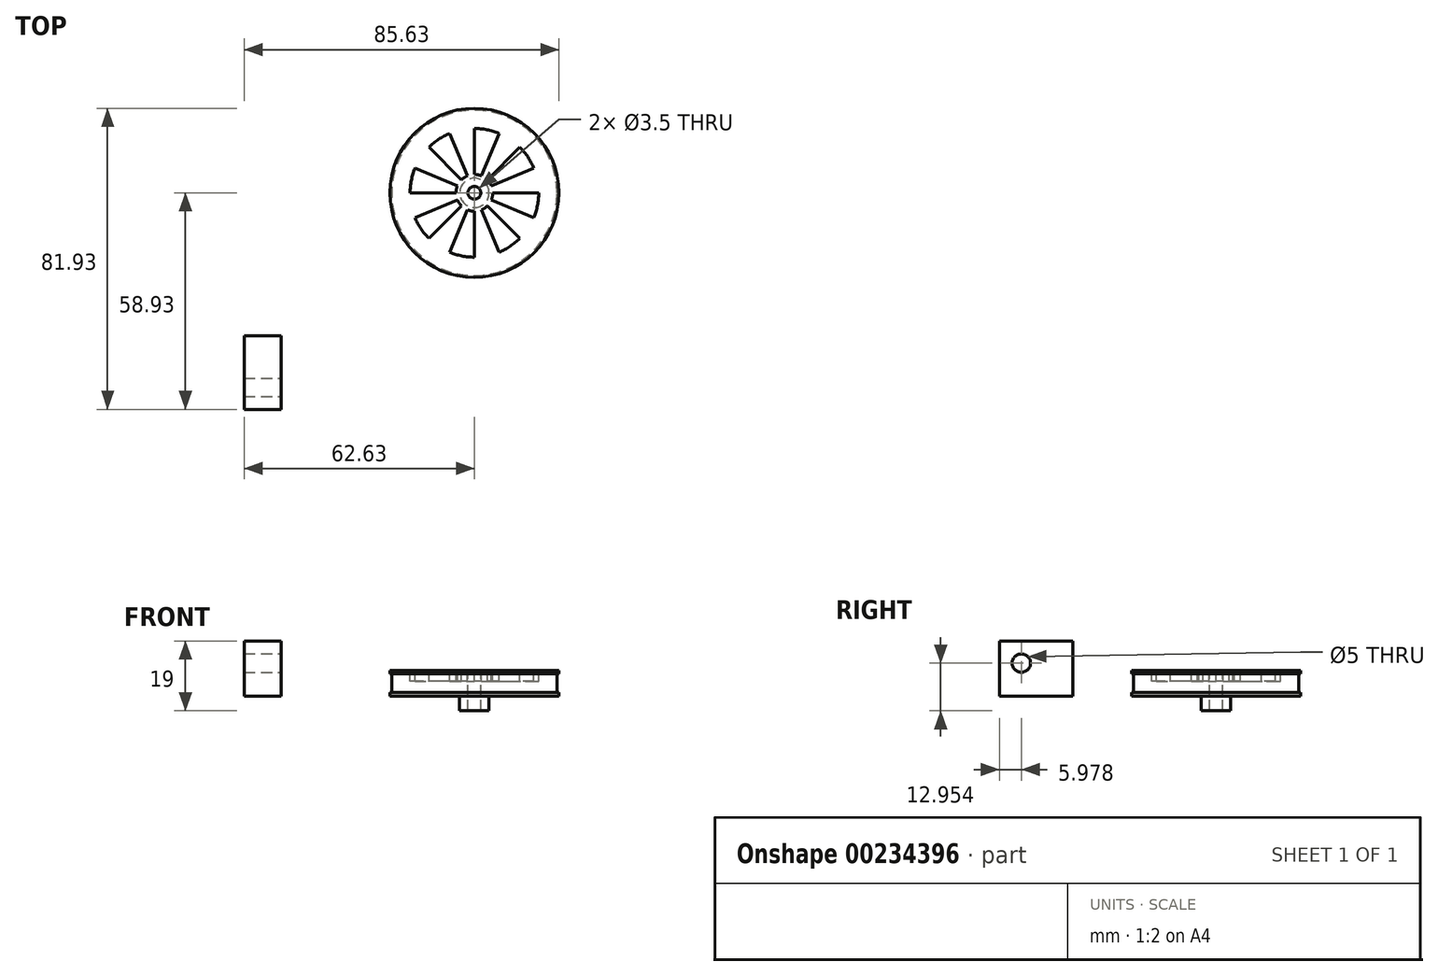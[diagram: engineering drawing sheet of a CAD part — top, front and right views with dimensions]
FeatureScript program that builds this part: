
annotation { "Feature Type Name" : "Feature", "Feature Type Description" : "" }
export const myFeature = defineFeature(function(context is Context, id is Id, definition is map)
    precondition{}
    {
        {
            var Q0;
            Q0=qCreatedBy(makeId("Top.planeOp"),FACE);
            var sketch = newSketch(context, id + "F0", { "sketchPlane" : qUnion([Q0])});
            skCircle(sketch, "E0", {"center": v(0, 0) * mm, "radius": 23 * mm});
            skSolve(sketch);
        }
        {
            var Q0;
            Q0=makeQuery(id+"F0.imprint","IMPRINT",FACE,{"disambiguationData":[TD([[makeQuery(id+"F0.imprint","IMPRINT",EDGE,{"derivedFrom":sQuery(id+"F0.wireOp",EDGE,"E0")}),1.0]])]});
            extrude(context, id + "F1", {"entities" : qUnion([Q0]), "depth" : 1 * mm});
        }
        {
            var Q0;
            Q0=makeQuery(id+"F1.opExtrude","CAP_FACE",FACE,{"disambiguationData":[OSD([sQuery(id+"F0.wireOp",EDGE,"E0")])],"isStart":false});
            var sketch = newSketch(context, id + "F2", { "sketchPlane" : qUnion([Q0])});
            skCircle(sketch, "E1", {"center": v(0, 0) * mm, "radius": 23 * mm});
            skCircle(sketch, "E2", {"center": v(0, 0) * mm, "radius": 22.5 * mm});
            skSolve(sketch);
        }
        {
            var Q0;
            Q0=makeQuery(id+"F2.imprint","IMPRINT",FACE,{"disambiguationData":[TD([[makeQuery(id+"F2.imprint","IMPRINT",EDGE,{"derivedFrom":sQuery(id+"F2.wireOp",EDGE,"E2")}),1.0]])]});
            extrude(context, id + "F3", {"entities" : qUnion([Q0]), "operationType" : NewBodyOperationType.ADD, "depth" : 5 * mm});
        }
        {
            var Q0;
            Q0=makeQuery(id+"F3.opExtrude","CAP_FACE",FACE,{"disambiguationData":[OSD([sQuery(id+"F2.wireOp",EDGE,"E2")])],"isStart":false});
            var sketch = newSketch(context, id + "F4", { "sketchPlane" : qUnion([Q0])});
            skCircle(sketch, "E3.0.0", {"center": v(0, 0) * mm, "radius": 22.5 * mm});
            skCircle(sketch, "E4", {"center": v(0, 0) * mm, "radius": 23 * mm});
            skSolve(sketch);
        }
        {
            var Q0;
            Q0=makeQuery(id+"F4.imprint","IMPRINT",FACE,{"disambiguationData":[TD([[makeQuery(id+"F4.imprint","IMPRINT",EDGE,{"derivedFrom":sQuery(id+"F4.wireOp",EDGE,"E3.0.0")}),-1.0]])]});
            var Q1;
            Q1=makeQuery(id+"F4.imprint","IMPRINT",FACE,{"disambiguationData":[TD([[makeQuery(id+"F4.imprint","IMPRINT",EDGE,{"derivedFrom":sQuery(id+"F4.wireOp",EDGE,"E3.0.0")}),1.0]])]});
            extrude(context, id + "F5", {"entities" : qUnion([Q0, Q1]), "operationType" : NewBodyOperationType.ADD, "depth" : 1 * mm});
        }
        {
            var Q0;
            Q0=makeQuery(id+"F5.opExtrude","CAP_FACE",FACE,{"disambiguationData":[OSD([sQuery(id+"F4.wireOp",EDGE,"E4")])],"isStart":false});
            var sketch = newSketch(context, id + "F6", { "sketchPlane" : qUnion([Q0])});
            skCircle(sketch, "E5.0.0", {"center": v(0, 0) * mm, "radius": 23 * mm});
            skCircle(sketch, "E6", {"center": v(0, 0) * mm, "radius": 1.75 * mm});
            skSolve(sketch);
        }
        {
            var Q0;
            Q0=makeQuery(id+"F6.imprint","IMPRINT",FACE,{"disambiguationData":[TD([[makeQuery(id+"F6.imprint","IMPRINT",EDGE,{"derivedFrom":sQuery(id+"F6.wireOp",EDGE,"E6")}),1.0]])]});
            extrude(context, id + "F7", {"entities" : qUnion([Q0]), "operationType" : NewBodyOperationType.REMOVE, "oppositeDirection" : true, "depth" : 25 * mm});
        }
        {
            var Q0;
            Q0=makeQuery(id+"F5.opExtrude","CAP_FACE",FACE,{"disambiguationData":[OSD([sQuery(id+"F4.wireOp",EDGE,"E4")])],"isStart":false});
            var sketch = newSketch(context, id + "F8", { "sketchPlane" : qUnion([Q0])});
            skCircle(sketch, "E7.0.0", {"center": v(0, 0) * mm, "radius": 23 * mm});
            skCircle(sketch, "E8", {"center": v(0, 0) * mm, "radius": 5 * mm});
            skCircle(sketch, "E9", {"center": v(0, 0) * mm, "radius": 17.5 * mm});
            skLineSegment(sketch, "E10", {"start": v(0, 0) * mm, "end": v(0, 17.5) * mm});
            skLineSegment(sketch, "E11", {"start": v(0, 0) * mm, "end": v(6.7, 16.17) * mm});
            skLineSegment(sketch, "E12", {"start": v(0, 0) * mm, "end": v(-6.7, 16.17) * mm});
            skLineSegment(sketch, "E13", {"start": v(0, 0) * mm, "end": v(-12.37, 12.37) * mm});
            skLineSegment(sketch, "E14", {"start": v(0, 0) * mm, "end": v(-16.17, 6.7) * mm});
            skLineSegment(sketch, "E15", {"start": v(0, 0) * mm, "end": v(-17.5, 0) * mm});
            skLineSegment(sketch, "E16", {"start": v(0, 0) * mm, "end": v(-16.17, -6.7) * mm});
            skLineSegment(sketch, "E17", {"start": v(0, 0) * mm, "end": v(-12.37, -12.37) * mm});
            skLineSegment(sketch, "E18", {"start": v(0, 0) * mm, "end": v(-6.7, -16.17) * mm});
            skLineSegment(sketch, "E19", {"start": v(0, 0) * mm, "end": v(0, -17.5) * mm});
            skLineSegment(sketch, "E20", {"start": v(0, 0) * mm, "end": v(6.7, -16.17) * mm});
            skLineSegment(sketch, "E21", {"start": v(0, 0) * mm, "end": v(12.37, -12.37) * mm});
            skLineSegment(sketch, "E22", {"start": v(0, 0) * mm, "end": v(16.17, -6.7) * mm});
            skLineSegment(sketch, "E23", {"start": v(0, 0) * mm, "end": v(17.5, 0) * mm});
            skLineSegment(sketch, "E24", {"start": v(0, 0) * mm, "end": v(16.17, 6.7) * mm});
            skLineSegment(sketch, "E25", {"start": v(0, 0) * mm, "end": v(12.37, 12.37) * mm});
            skSolve(sketch);
        }
        {
            var Q0;
            {var subQ0=sQuery(id+"F8.wireOp",EDGE,"E10");var subQ1=sQuery(id+"F8.wireOp",EDGE,"E8");var subQ2=makeQuery(id+"F8.imprint","INTERSECT",VERTEX,{"derivedFrom":[subQ1,subQ0]});Q0=makeQuery(id+"F8.imprint","IMPRINT",FACE,{"disambiguationData":[TD([[makeQuery(id+"F8.imprint","IMPRINT",EDGE,{"disambiguationData":[TD([[subQ2,1.0]])],"derivedFrom":subQ1}),-1.0]])]});}
            var Q1;
            {var subQ0=sQuery(id+"F8.wireOp",EDGE,"E24");var subQ1=sQuery(id+"F8.wireOp",EDGE,"E8");var subQ2=makeQuery(id+"F8.imprint","INTERSECT",VERTEX,{"derivedFrom":[subQ1,subQ0]});Q1=makeQuery(id+"F8.imprint","IMPRINT",FACE,{"disambiguationData":[TD([[makeQuery(id+"F8.imprint","IMPRINT",EDGE,{"disambiguationData":[TD([[subQ2,-1.0]])],"derivedFrom":subQ1}),-1.0]])]});}
            var Q2;
            {var subQ0=sQuery(id+"F8.wireOp",EDGE,"E23");var subQ1=sQuery(id+"F8.wireOp",EDGE,"E8");var subQ2=makeQuery(id+"F8.imprint","INTERSECT",VERTEX,{"derivedFrom":[subQ1,subQ0]});Q2=makeQuery(id+"F8.imprint","IMPRINT",FACE,{"disambiguationData":[TD([[makeQuery(id+"F8.imprint","IMPRINT",EDGE,{"disambiguationData":[TD([[subQ2,1.0]])],"derivedFrom":subQ1}),-1.0]])]});}
            var Q3;
            {var subQ0=sQuery(id+"F8.wireOp",EDGE,"E20");var subQ1=sQuery(id+"F8.wireOp",EDGE,"E8");var subQ2=makeQuery(id+"F8.imprint","INTERSECT",VERTEX,{"derivedFrom":[subQ1,subQ0]});Q3=makeQuery(id+"F8.imprint","IMPRINT",FACE,{"disambiguationData":[TD([[makeQuery(id+"F8.imprint","IMPRINT",EDGE,{"disambiguationData":[TD([[subQ2,-1.0]])],"derivedFrom":subQ1}),-1.0]])]});}
            var Q4;
            {var subQ0=sQuery(id+"F8.wireOp",EDGE,"E18");var subQ1=sQuery(id+"F8.wireOp",EDGE,"E8");var subQ2=makeQuery(id+"F8.imprint","INTERSECT",VERTEX,{"derivedFrom":[subQ1,subQ0]});Q4=makeQuery(id+"F8.imprint","IMPRINT",FACE,{"disambiguationData":[TD([[makeQuery(id+"F8.imprint","IMPRINT",EDGE,{"disambiguationData":[TD([[subQ2,-1.0]])],"derivedFrom":subQ1}),-1.0]])]});}
            var Q5;
            {var subQ0=sQuery(id+"F8.wireOp",EDGE,"E16");var subQ1=sQuery(id+"F8.wireOp",EDGE,"E8");var subQ2=makeQuery(id+"F8.imprint","INTERSECT",VERTEX,{"derivedFrom":[subQ1,subQ0]});Q5=makeQuery(id+"F8.imprint","IMPRINT",FACE,{"disambiguationData":[TD([[makeQuery(id+"F8.imprint","IMPRINT",EDGE,{"disambiguationData":[TD([[subQ2,-1.0]])],"derivedFrom":subQ1}),-1.0]])]});}
            var Q6;
            {var subQ0=sQuery(id+"F8.wireOp",EDGE,"E14");var subQ1=sQuery(id+"F8.wireOp",EDGE,"E8");var subQ2=makeQuery(id+"F8.imprint","INTERSECT",VERTEX,{"derivedFrom":[subQ1,subQ0]});Q6=makeQuery(id+"F8.imprint","IMPRINT",FACE,{"disambiguationData":[TD([[makeQuery(id+"F8.imprint","IMPRINT",EDGE,{"disambiguationData":[TD([[subQ2,-1.0]])],"derivedFrom":subQ1}),-1.0]])]});}
            var Q7;
            {var subQ0=sQuery(id+"F8.wireOp",EDGE,"E12");var subQ1=sQuery(id+"F8.wireOp",EDGE,"E8");var subQ2=makeQuery(id+"F8.imprint","INTERSECT",VERTEX,{"derivedFrom":[subQ1,subQ0]});Q7=makeQuery(id+"F8.imprint","IMPRINT",FACE,{"disambiguationData":[TD([[makeQuery(id+"F8.imprint","IMPRINT",EDGE,{"disambiguationData":[TD([[subQ2,-1.0]])],"derivedFrom":subQ1}),-1.0]])]});}
            extrude(context, id + "F9", {"entities" : qUnion([Q0, Q1, Q2, Q3, Q4, Q5, Q6, Q7]), "operationType" : NewBodyOperationType.REMOVE, "oppositeDirection" : true, "depth" : 3 * mm});
        }
        {
            var Q0;
            Q0=makeQuery(id+"F1.opExtrude","CAP_FACE",FACE,{"disambiguationData":[OSD([sQuery(id+"F0.wireOp",EDGE,"E0")])],"isStart":true});
            var sketch = newSketch(context, id + "F10", { "sketchPlane" : qUnion([Q0])});
            skCircle(sketch, "E26", {"center": v(0, 0) * mm, "radius": 4 * mm});
            skSolve(sketch);
        }
        {
            var Q0;
            Q0=makeQuery(id+"F10.imprint","IMPRINT",FACE,{"disambiguationData":[TD([[makeQuery(id+"F10.imprint","IMPRINT",EDGE,{"derivedFrom":sQuery(id+"F10.wireOp",EDGE,"E26")}),1.0]])]});
            extrude(context, id + "F11", {"entities" : qUnion([Q0]), "depth" : 4 * mm});
        }
        {
            var Q0;
            Q0=qCreatedBy(makeId("Top.planeOp"),FACE);
            var sketch = newSketch(context, id + "F12", { "sketchPlane" : qUnion([Q0])});
            skLineSegment(sketch, "E27.bottom", {"start": v(-62.63, -58.93) * mm, "end": v(-52.63, -58.93) * mm});
            skLineSegment(sketch, "E27.top", {"start": v(-62.63, -38.93) * mm, "end": v(-52.63, -38.93) * mm});
            skLineSegment(sketch, "E27.left", {"start": v(-62.63, -58.93) * mm, "end": v(-62.63, -38.93) * mm});
            skLineSegment(sketch, "E27.right", {"start": v(-52.63, -58.93) * mm, "end": v(-52.63, -38.93) * mm});
            skSolve(sketch);
        }
        {
            var Q0;
            Q0=makeQuery(id+"F12.imprint","IMPRINT",FACE,{"disambiguationData":[TD([[makeQuery(id+"F12.imprint","IMPRINT",EDGE,{"derivedFrom":sQuery(id+"F12.wireOp",EDGE,"E27.bottom")}),1.0]])]});
            extrude(context, id + "F13", {"entities" : qUnion([Q0]), "depth" : 15 * mm});
        }
        {
            var Q0;
            Q0=makeQuery(id+"F13.opExtrude","SWEPT_FACE",FACE,{"disambiguationData":[OSD([sQuery(id+"F12.wireOp",EDGE,"E27.right")])]});
            var sketch = newSketch(context, id + "F14", { "sketchPlane" : qUnion([Q0])});
            skCircle(sketch, "E28", {"center": v(-52.95, 8.95) * mm, "radius": 2.5 * mm});
            skSolve(sketch);
        }
        {
            var Q0;
            Q0=makeQuery(id+"F14.imprint","IMPRINT",FACE,{"disambiguationData":[TD([[makeQuery(id+"F14.imprint","IMPRINT",EDGE,{"derivedFrom":sQuery(id+"F14.wireOp",EDGE,"E28")}),1.0]])]});
            extrude(context, id + "F15", {"entities" : qUnion([Q0]), "operationType" : NewBodyOperationType.REMOVE, "oppositeDirection" : true, "depth" : 25 * mm});
        }
    });
